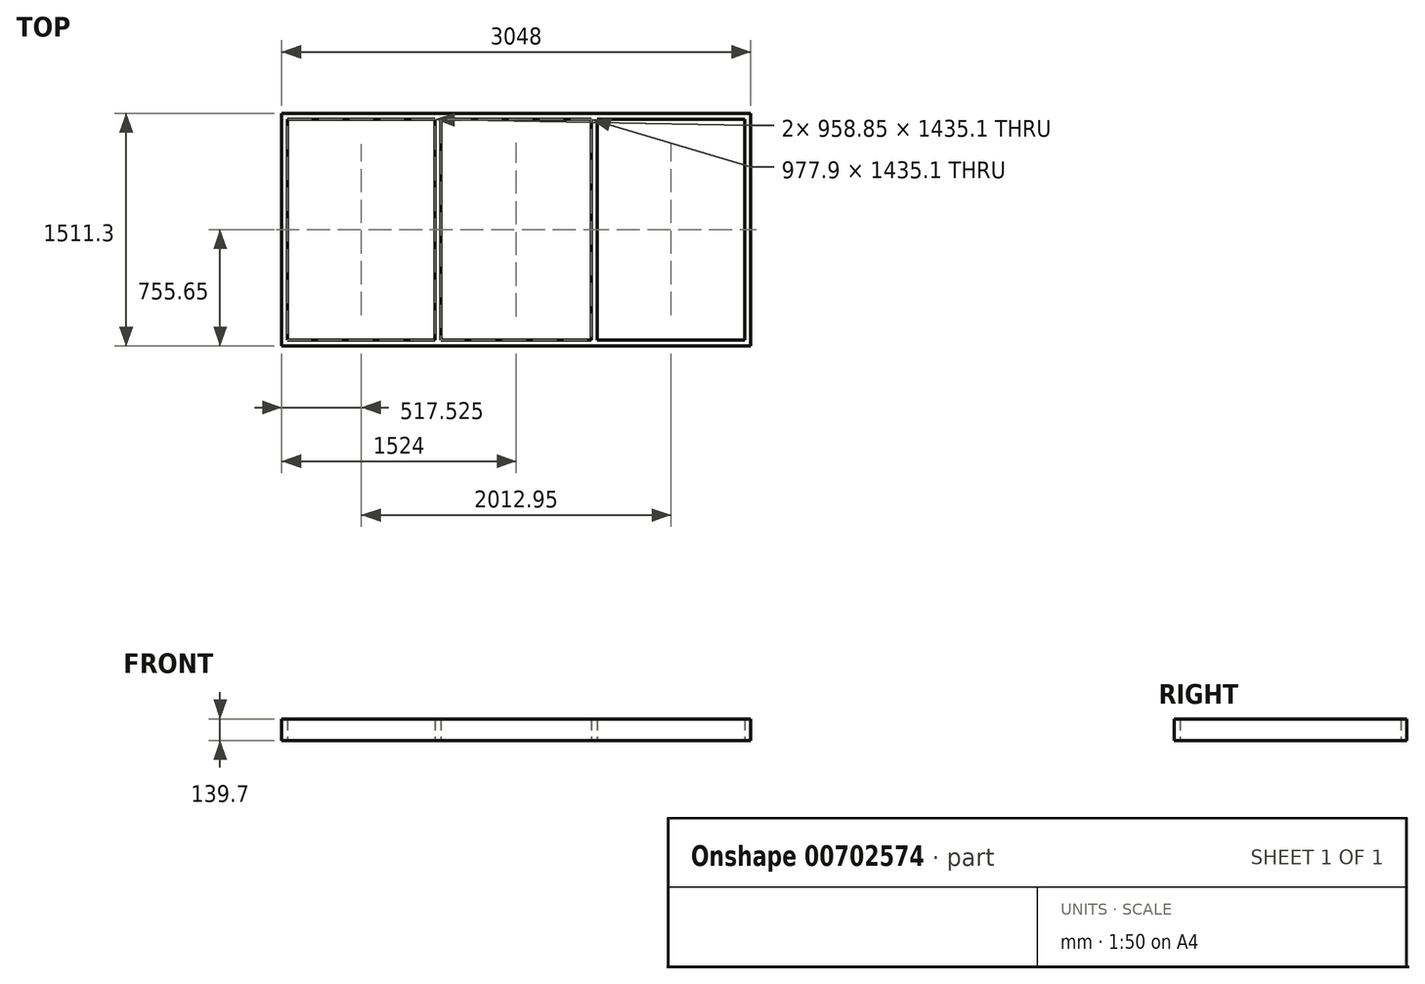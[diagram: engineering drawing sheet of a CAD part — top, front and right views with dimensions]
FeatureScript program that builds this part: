
annotation { "Feature Type Name" : "Feature", "Feature Type Description" : "" }
export const myFeature = defineFeature(function(context is Context, id is Id, definition is map)
    precondition{}
    {
        {
            var Q0;
            Q0=qCreatedBy(makeId("Top.planeOp"),FACE);
            var sketch = newSketch(context, id + "F0", { "sketchPlane" : qUnion([Q0])});
            skLineSegment(sketch, "E0.left", {"start": v(1524, 755.65) * mm, "end": v(1524, -755.65) * mm});
            skLineSegment(sketch, "E0.right", {"start": v(-1524, 755.65) * mm, "end": v(-1524, -755.65) * mm});
            skPoint(sketch, "E0.middle", {"position": v(0, 0) * mm});
            skLineSegment(sketch, "E1", {"start": v(-1524, 755.65) * mm, "end": v(-1485.9, 755.65) * mm});
            skLineSegment(sketch, "E2", {"start": v(-1485.9, 717.55) * mm, "end": v(-1485.9, -717.55) * mm});
            skLineSegment(sketch, "E3", {"start": v(-1485.9, -755.65) * mm, "end": v(-1524, -755.65) * mm});
            skLineSegment(sketch, "E4", {"start": v(1524, 755.65) * mm, "end": v(1485.9, 755.65) * mm});
            skLineSegment(sketch, "E5", {"start": v(1485.9, 717.55) * mm, "end": v(1485.9, -717.55) * mm});
            skLineSegment(sketch, "E6", {"start": v(1485.9, -755.65) * mm, "end": v(1524, -755.65) * mm});
            skLineSegment(sketch, "E7", {"start": v(-1485.9, 755.65) * mm, "end": v(1485.9, 755.65) * mm});
            skLineSegment(sketch, "E8", {"start": v(-1485.9, -755.65) * mm, "end": v(1485.9, -755.65) * mm});
            skLineSegment(sketch, "E9", {"start": v(-527.05, -717.55) * mm, "end": v(-527.05, 717.55) * mm});
            skLineSegment(sketch, "E10", {"start": v(527.05, -717.55) * mm, "end": v(527.05, 717.55) * mm});
            skLineSegment(sketch, "E11", {"start": v(-488.95, -717.55) * mm, "end": v(-488.95, 717.55) * mm});
            skLineSegment(sketch, "E12", {"start": v(488.95, -717.55) * mm, "end": v(488.95, 717.55) * mm});
            skLineSegment(sketch, "E13", {"start": v(-1524, 717.55) * mm, "end": v(1524, 717.55) * mm});
            skLineSegment(sketch, "E14", {"start": v(-1524, -717.55) * mm, "end": v(1524, -717.55) * mm});
            skSolve(sketch);
        }
        {
            var Q0;
            Q0 = qSketchRegion(id + "F0", true);
            var Q1;
            {var subQ0=sQuery(id+"F0.wireOp",EDGE,"E9");Q1=makeQuery(id+"F0.imprint","IMPRINT",FACE,{"disambiguationData":[TD([[makeQuery(id+"F0.imprint","IMPRINT",EDGE,{"derivedFrom":subQ0}),-1.0]])]});}
            var Q2;
            {var subQ0=sQuery(id+"F0.wireOp",EDGE,"E10");Q2=makeQuery(id+"F0.imprint","IMPRINT",FACE,{"disambiguationData":[TD([[makeQuery(id+"F0.imprint","IMPRINT",EDGE,{"derivedFrom":subQ0}),1.0]])]});}
            extrude(context, id + "F1", {"entities" : qUnion([Q0, Q1, Q2]), "endBound" : BoundingType.SYMMETRIC, "depth" : 139.7 * mm, "offsetDistance" : 25.4 * mm});
        }
    });
